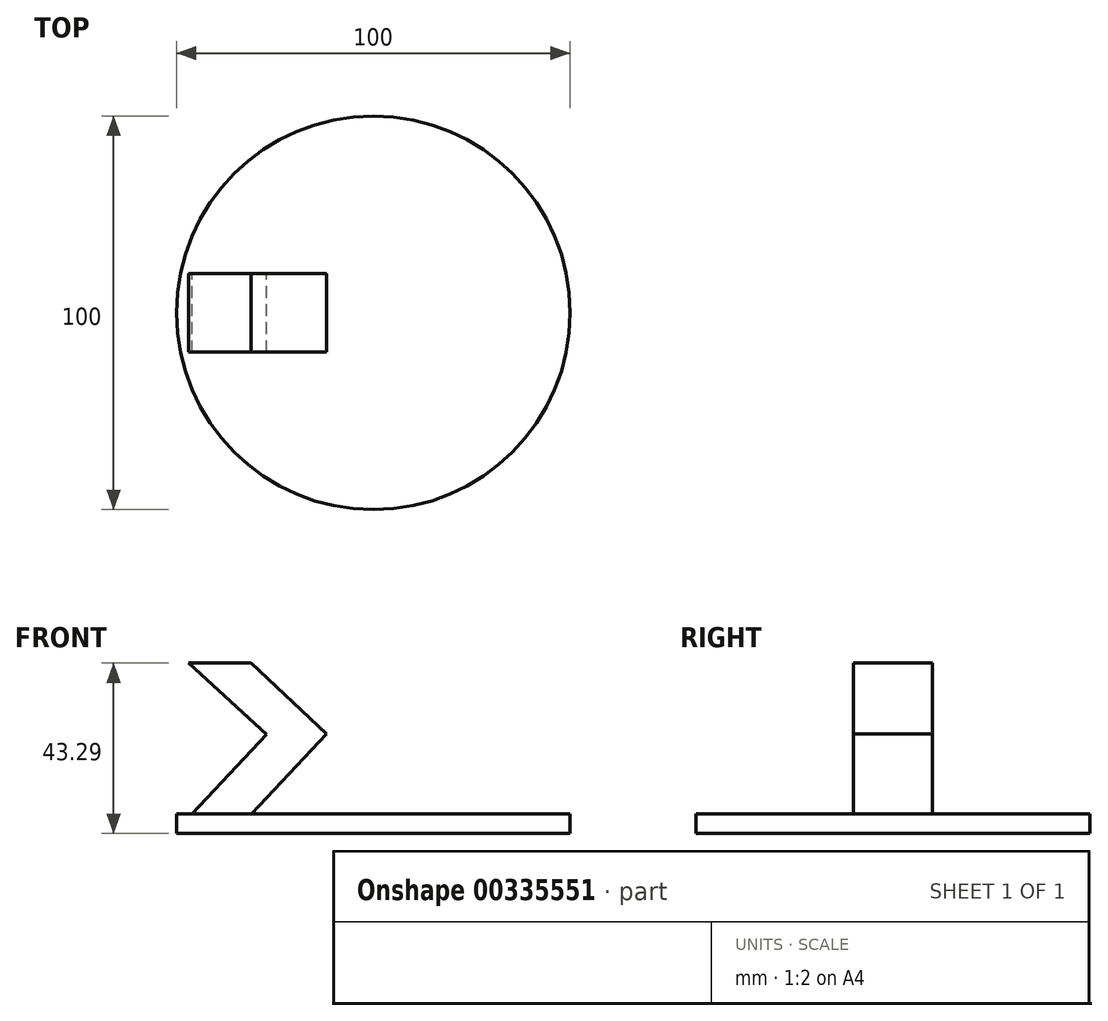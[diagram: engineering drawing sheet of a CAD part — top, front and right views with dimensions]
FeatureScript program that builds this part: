
annotation { "Feature Type Name" : "Feature", "Feature Type Description" : "" }
export const myFeature = defineFeature(function(context is Context, id is Id, definition is map)
    precondition{}
    {
        {
            var Q0;
            Q0=qCreatedBy(makeId("Top.planeOp"),FACE);
            var sketch = newSketch(context, id + "F0", { "sketchPlane" : qUnion([Q0])});
            skCircle(sketch, "E0", {"center": v(0, 0) * mm, "radius": 50 * mm});
            skSolve(sketch);
        }
        {
            var Q0;
            Q0=makeQuery(id+"F0.imprint","IMPRINT",FACE,{"disambiguationData":[TD([[makeQuery(id+"F0.imprint","IMPRINT",EDGE,{"derivedFrom":sQuery(id+"F0.wireOp",EDGE,"E0")}),1.0]])]});
            var sketch = newSketch(context, id + "F1", { "sketchPlane" : qUnion([Q0])});
            skSolve(sketch);
        }
        {
            var Q0;
            Q0=makeQuery(id+"F1.imprint","IMPRINT",FACE,{"disambiguationData":[TD([[makeQuery(id+"F1.imprint","IMPRINT",EDGE,{"derivedFrom":makeQuery(id+"F0.imprint","IMPRINT",EDGE,{"derivedFrom":sQuery(id+"F0.wireOp",EDGE,"E0")})}),1.0]])]});
            var sketch = newSketch(context, id + "F2", { "sketchPlane" : qUnion([Q0])});
            skSolve(sketch);
        }
        {
            var Q0;
            Q0=makeQuery(id+"F2.imprint","IMPRINT",FACE,{"disambiguationData":[TD([[makeQuery(id+"F2.imprint","IMPRINT",EDGE,{"derivedFrom":makeQuery(id+"F1.imprint","IMPRINT",EDGE,{"derivedFrom":makeQuery(id+"F0.imprint","IMPRINT",EDGE,{"derivedFrom":sQuery(id+"F0.wireOp",EDGE,"E0")})})}),1.0]])]});
            extrude(context, id + "F3", {"entities" : qUnion([Q0]), "depth" : 5 * mm});
        }
        {
            var Q0;
            Q0=qCreatedBy(makeId("Front.planeOp"),FACE);
            var sketch = newSketch(context, id + "F4", { "sketchPlane" : qUnion([Q0])});
            skLineSegment(sketch, "E1", {"start": v(-46.07, 5) * mm, "end": v(-27.13, 25.14) * mm});
            skLineSegment(sketch, "E2", {"start": v(-27.13, 25.14) * mm, "end": v(-46.89, 43.29) * mm});
            skLineSegment(sketch, "E3", {"start": v(-46.89, 43.29) * mm, "end": v(-31.07, 43.29) * mm});
            skLineSegment(sketch, "E4", {"start": v(-31.07, 43.29) * mm, "end": v(-11.92, 25.28) * mm});
            skLineSegment(sketch, "E5", {"start": v(-11.92, 25.28) * mm, "end": v(-30.99, 5) * mm});
            skLineSegment(sketch, "E6", {"start": v(-46.07, 5) * mm, "end": v(-30.99, 5) * mm});
            skSolve(sketch);
        }
        {
            var Q0;
            Q0=makeQuery(id+"F4.imprint","IMPRINT",FACE,{"disambiguationData":[TD([[makeQuery(id+"F4.imprint","IMPRINT",EDGE,{"derivedFrom":sQuery(id+"F4.wireOp",EDGE,"E1")}),-1.0]])]});
            var sketch = newSketch(context, id + "F5", { "sketchPlane" : qUnion([Q0])});
            skLineSegment(sketch, "E7", {"start": v(0, 45.48) * mm, "end": v(0, 16.33) * mm});
            skSolve(sketch);
        }
        {
            var Q0;
            Q0=makeQuery(id+"F5.imprint","IMPRINT",FACE,{"disambiguationData":[TD([[makeQuery(id+"F5.imprint","IMPRINT",EDGE,{"derivedFrom":makeQuery(id+"F4.imprint","IMPRINT",EDGE,{"derivedFrom":sQuery(id+"F4.wireOp",EDGE,"E1")})}),-1.0]])]});
            extrude(context, id + "F6", {"entities" : qUnion([Q0]), "operationType" : NewBodyOperationType.ADD, "endBound" : BoundingType.SYMMETRIC, "depth" : 20 * mm});
        }
    });
